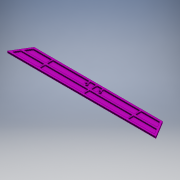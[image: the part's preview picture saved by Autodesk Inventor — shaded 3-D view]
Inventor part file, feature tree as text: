
AUTODESK INVENTOR PART (.ipt)
format: ipt  version: 2016 (Build 200138000, 138)  size: 310,784 bytes
history: native  units: mm
features: extrude x5, fillet x3, other x1, sketch x1, hole x1
ambient origin geometry x8: Origin, YZ Plane, XZ Plane, XY Plane, X Axis, Y Axis, Z Axis, Center Point
bodies: Body1 (feature_tree)
feature tree (11):
  other  "ソリッド1"
  sketch  "スケッチ1"
  extrude  "押し出し1"  Depth=29.0mm
  extrude  "押し出し2"  Depth=325.0mm
  extrude  "押し出し3"  Depth=3.0mm
  hole  "穴1"  [1 undecoded]
  fillet  "フィレット1"  Radius=2.0mm
  extrude  "押し出し4"  Depth=2.0mm
  extrude  "押し出し5"  Depth=2.0mm
  fillet  "フィレット3"  Radius=158.5mm
  fillet  "フィレット4"  Radius=158.5mm
note: 1 required parameter value undecoded (feature->parameter linkage not recoverable at this tier; creation-order binding heuristic only, values carry confidence <= 0.55)
